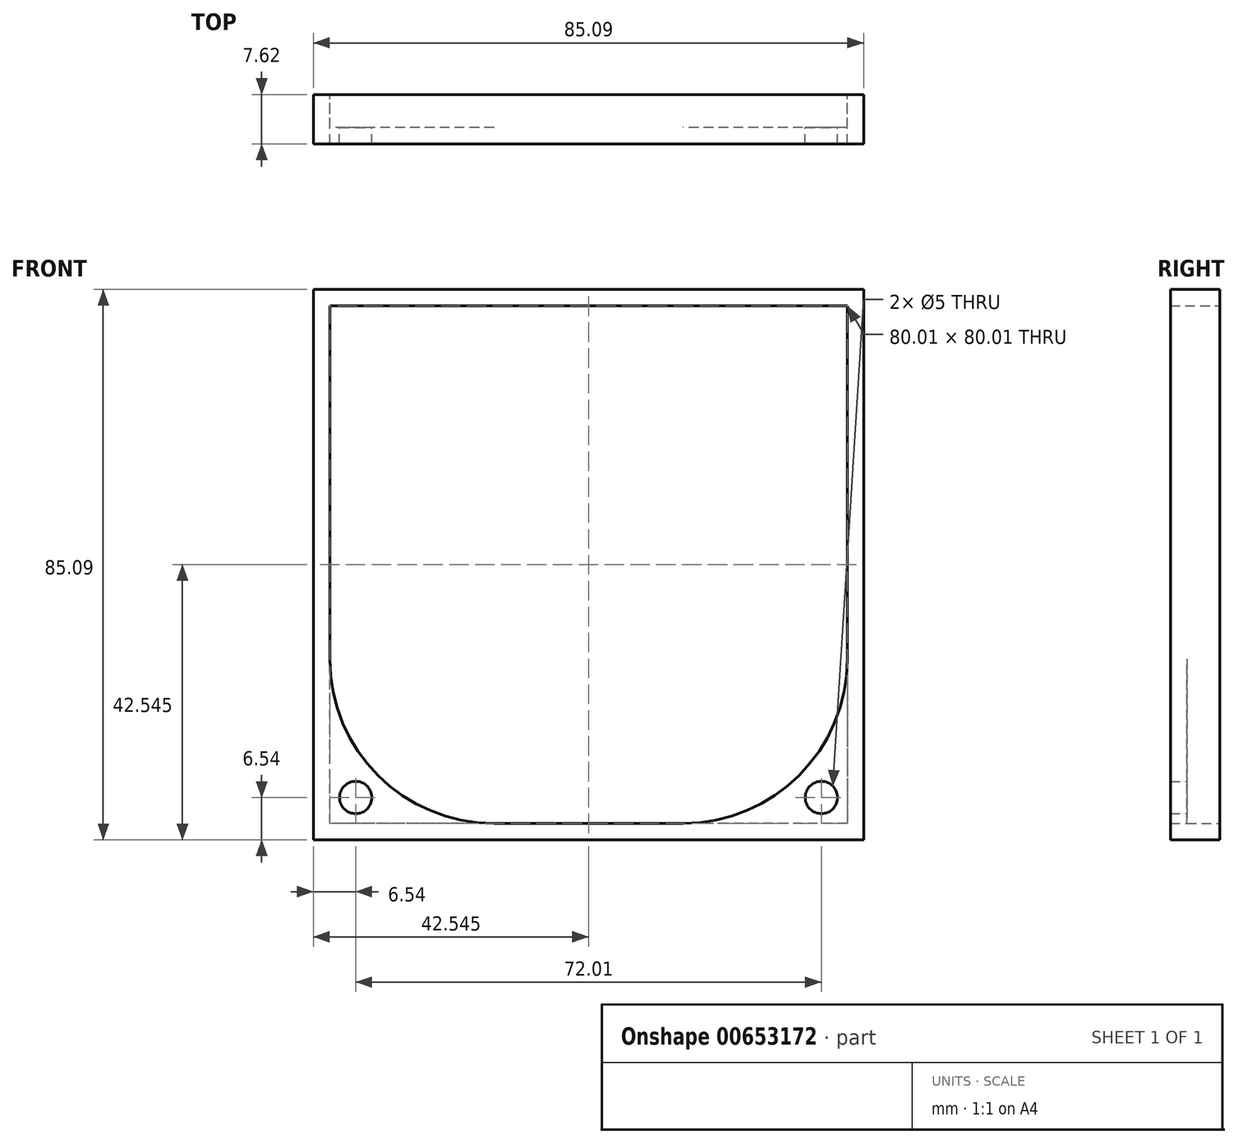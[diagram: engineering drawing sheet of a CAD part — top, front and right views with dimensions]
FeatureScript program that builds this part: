
annotation { "Feature Type Name" : "Feature", "Feature Type Description" : "" }
export const myFeature = defineFeature(function(context is Context, id is Id, definition is map)
    precondition{}
    {
        {
            var Q0;
            Q0=qCreatedBy(makeId("Front.planeOp"),FACE);
            var sketch = newSketch(context, id + "F0", { "sketchPlane" : qUnion([Q0])});
            skLineSegment(sketch, "E0", {"start": v(0, 25.4) * mm, "end": v(0, 80.01) * mm});
            skLineSegment(sketch, "E1", {"start": v(0, 80.01) * mm, "end": v(80.01, 80.01) * mm});
            skLineSegment(sketch, "E2", {"start": v(80.01, 80.01) * mm, "end": v(80.01, 25.4) * mm});
            skLineSegment(sketch, "E3", {"start": v(54.61, 0) * mm, "end": v(25.4, 0) * mm});
            skLineSegment(sketch, "E4.bottom", {"start": v(-2.54, 82.55) * mm, "end": v(82.55, 82.55) * mm});
            skLineSegment(sketch, "E4.top", {"start": v(-2.54, -2.54) * mm, "end": v(82.55, -2.54) * mm});
            skLineSegment(sketch, "E4.left", {"start": v(-2.54, 82.55) * mm, "end": v(-2.54, -2.54) * mm});
            skLineSegment(sketch, "E4.right", {"start": v(82.55, 82.55) * mm, "end": v(82.55, -2.54) * mm});
            skPoint(sketch, "E5.visualSharp", {"position": v(80.01, 0) * mm});
            skArc(sketch, "E5.filletArc", {"start": v(54.61, 0) * mm, "mid": v(72.57, 7.44) * mm, "end": v(80.01, 25.4) * mm});
            skPoint(sketch, "E6.visualSharp", {"position": v(0, 0) * mm});
            skArc(sketch, "E6.filletArc", {"start": v(0, 25.4) * mm, "mid": v(7.44, 7.44) * mm, "end": v(25.4, 0) * mm});
            skCircle(sketch, "E7", {"center": v(4, 4) * mm, "radius": 2.5 * mm});
            skLineSegment(sketch, "E8", {"start": v(40, 80.01) * mm, "end": v(40, 0) * mm, "construction": true});
            skCircle(sketch, "E9.MirrorC", {"center": v(76, 4) * mm, "radius": 2.5 * mm});
            skSolve(sketch);
        }
        {
            var Q0;
            Q0 = qSketchRegion(id + "F0", true);
            extrude(context, id + "F1", {"entities" : qUnion([Q0]), "depth" : 7.62 * mm, "offsetDistance" : 25.4 * mm});
        }
        {
            var Q0;
            Q0=makeQuery(id+"F1.opExtrude","CAP_FACE",FACE,{"disambiguationData":[OSD([sQuery(id+"F0.wireOp",EDGE,"E0"),sQuery(id+"F0.wireOp",EDGE,"E1"),sQuery(id+"F0.wireOp",EDGE,"E2"),sQuery(id+"F0.wireOp",EDGE,"E3"),sQuery(id+"F0.wireOp",EDGE,"E4.bottom"),sQuery(id+"F0.wireOp",EDGE,"E4.top"),sQuery(id+"F0.wireOp",EDGE,"E4.left"),sQuery(id+"F0.wireOp",EDGE,"E4.right"),sQuery(id+"F0.wireOp",EDGE,"E5.filletArc"),sQuery(id+"F0.wireOp",EDGE,"E6.filletArc"),sQuery(id+"F0.wireOp",EDGE,"E7"),sQuery(id+"F0.wireOp",EDGE,"E9.MirrorC")])],"isStart":true});
            var sketch = newSketch(context, id + "F2", { "sketchPlane" : qUnion([Q0])});
            skLineSegment(sketch, "E10.bottom", {"start": v(-80.01, 80.01) * mm, "end": v(0, 80.01) * mm});
            skLineSegment(sketch, "E10.top", {"start": v(-80.01, 0) * mm, "end": v(0, 0) * mm});
            skLineSegment(sketch, "E10.left", {"start": v(-80.01, 80.01) * mm, "end": v(-80.01, 0) * mm});
            skLineSegment(sketch, "E10.right", {"start": v(0, 80.01) * mm, "end": v(0, 0) * mm});
            skSolve(sketch);
        }
        {
            var Q0;
            Q0 = qSketchRegion(id + "F2", true);
            extrude(context, id + "F3", {"entities" : qUnion([Q0]), "operationType" : NewBodyOperationType.REMOVE, "oppositeDirection" : true, "depth" : 5.08 * mm, "offsetDistance" : 25.4 * mm});
        }
    });
